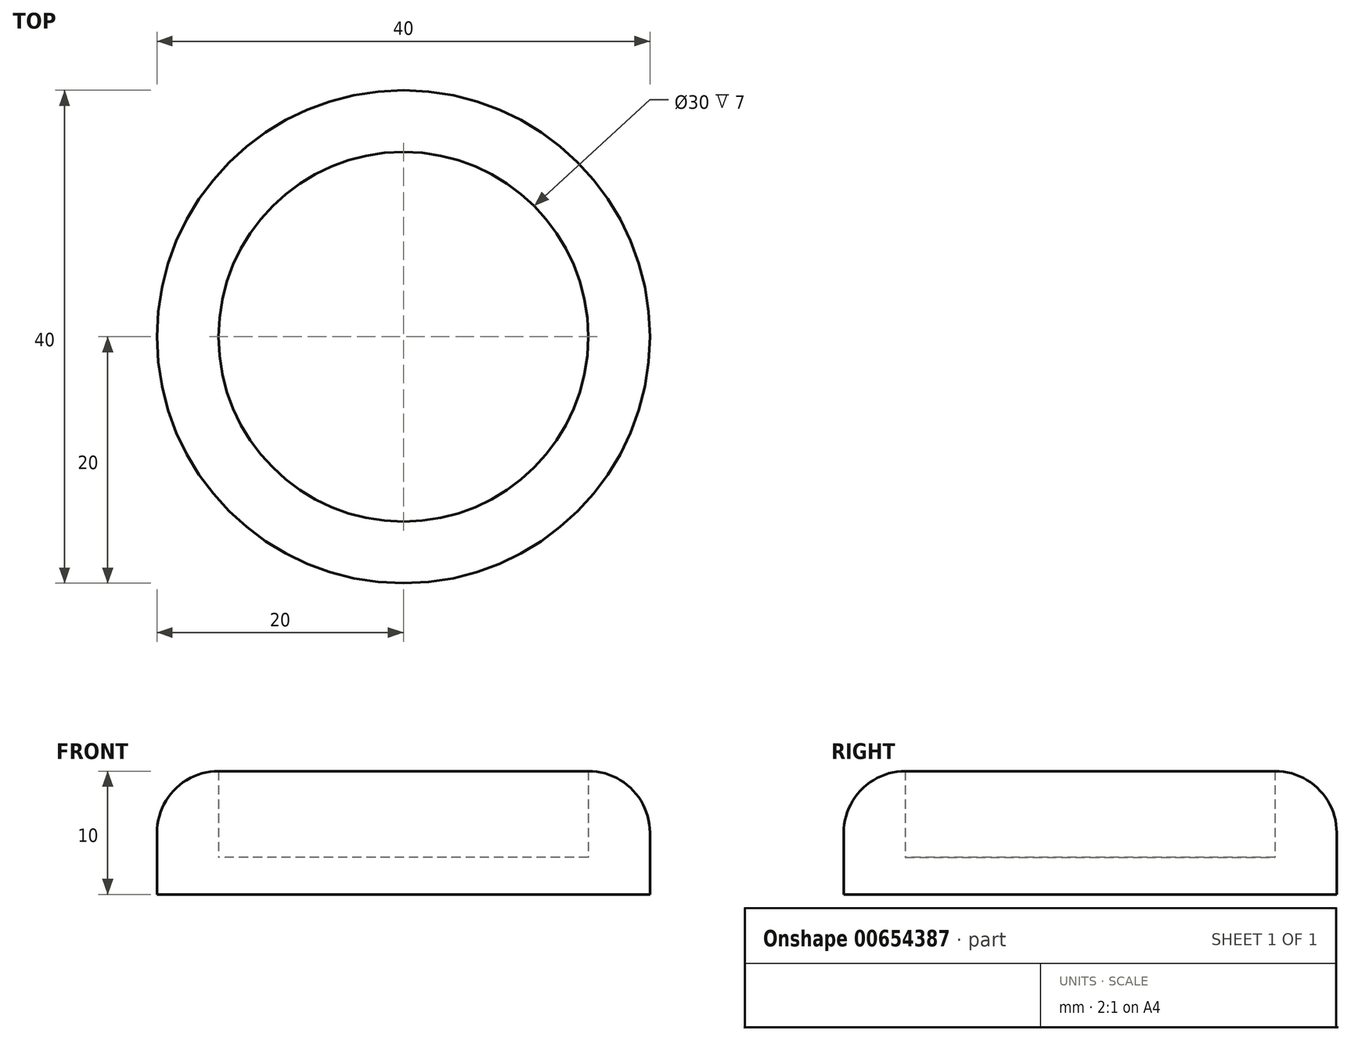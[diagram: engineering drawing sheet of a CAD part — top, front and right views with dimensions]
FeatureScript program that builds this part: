
annotation { "Feature Type Name" : "Feature", "Feature Type Description" : "" }
export const myFeature = defineFeature(function(context is Context, id is Id, definition is map)
    precondition{}
    {
        {
            var Q0;
            Q0=qCreatedBy(makeId("Top.planeOp"),FACE);
            var sketch = newSketch(context, id + "F0", { "sketchPlane" : qUnion([Q0])});
            skCircle(sketch, "E0", {"center": v(0, 0) * mm, "radius": 20 * mm});
            skCircle(sketch, "E1", {"center": v(0, 0) * mm, "radius": 15 * mm});
            skSolve(sketch);
        }
        {
            var Q0;
            Q0=makeQuery(id+"F0.imprint","IMPRINT",FACE,{"disambiguationData":[TD([[makeQuery(id+"F0.imprint","IMPRINT",EDGE,{"derivedFrom":sQuery(id+"F0.wireOp",EDGE,"E0")}),1.0]])]});
            extrude(context, id + "F1", {"entities" : qUnion([Q0]), "depth" : 7 * mm, "offsetDistance" : 25.4 * mm});
        }
        {
            var Q0;
            Q0=qCreatedBy(makeId("Top.planeOp"),FACE);
            var sketch = newSketch(context, id + "F2", { "sketchPlane" : qUnion([Q0])});
            skCircle(sketch, "E2", {"center": v(0, 0) * mm, "radius": 20 * mm});
            skSolve(sketch);
        }
        {
            var Q0;
            Q0=makeQuery(id+"F2.imprint","IMPRINT",FACE,{"disambiguationData":[TD([[makeQuery(id+"F2.imprint","IMPRINT",EDGE,{"derivedFrom":sQuery(id+"F2.wireOp",EDGE,"E2")}),1.0]])]});
            extrude(context, id + "F3", {"entities" : qUnion([Q0]), "operationType" : NewBodyOperationType.ADD, "oppositeDirection" : true, "depth" : 3 * mm, "offsetDistance" : 25 * mm});
        }
        {
            var Q0;
            Q0=makeQuery(id+"F1.opExtrude","CAP_EDGE",EDGE,{"disambiguationData":[OSD([sQuery(id+"F0.wireOp",EDGE,"E0")])],"isStart":false});
            fillet(context, id + "F4", {"entities" : qUnion([Q0]), "radius" : 5 * mm, "tangentPropagation" : true, "allowEdgeOverflow" : false});
        }
    });
